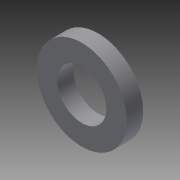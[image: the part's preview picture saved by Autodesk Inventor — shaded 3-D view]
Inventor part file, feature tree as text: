
AUTODESK INVENTOR PART (.ipt)
format: ipt  version: 2013 (Build 170138000, 138)  size: 77,824 bytes
history: native  units: in
note: dims shown in document units (in); Inventor stores cm internally (conversion verified against a paired STEP export)
features: extrude x1, sketch x1
ambient origin geometry x8: Origin, YZ Plane, XZ Plane, XY Plane, X Axis, Y Axis, Z Axis, Center Point
bodies: Solid1 (feature_tree)
feature tree (2):
  extrude  "Extrusion1"  Depth=0.375in
  sketch  "Sketch1"  dims[d0=0.6875in d1=0.375in d2=0.125in d3=0.0in]
